# Revit family: LeL Tago 3.0
name_source: partatom
category: Lighting Fixtures
units: mm (PartAtom-declared; Revit-internal decimal feet)

## family parameters
Always vertical = No
Cut with Voids When Loaded = No
Light Source = No
OmniClass Number = 23.80.70.00
OmniClass Title = Lighting
Part Type = Normal
Room Calculation Point = No
Round Connector Dimension = Use Diameter
Shared = No
Work Plane-Based = Yes

## types (7) — shared parameters
Apparent Load = 14 VA
CCT = 3000 K
CRI = CRI80
Default Elevation = 1219 mm
Description = Outdoor/linear profiles
Finish = LeL Black
IK = IK09
IP = IP65 IP67 IP69
Lamp = LED
Manufacturer = L&L Luce&Light srl
Model = TG30
Rated Power supply = 230 V
URL = https://www.lucelight.it
Wattage = 14 W
Weight = 1.08 kg
zero-valued in all types: Clips offset

## per-type parameters (varying)
| type | Lumen Output | Optic |
| 3.0 A 14W | 664 lm | TAGO Light source : 3.0 A 14W |
| 3.0 G 14W | 682 lm | TAGO Light source : 3.0 G 14W |
| 3.0 K 69° 14W | 919 lm | TAGO Light source : 3.0 K 69° 14W |
| 3.0 L 29° 14W | 932 lm | TAGO Light source : 3.0 L 29° 14W |
| 3.0 M 17° 14W | 838 lm | TAGO Light source : 3.0 M 17° 14W |
| 3.0 S 11° 14W | 739 lm | TAGO Light source : 3.0 S 11° 14W |
| 3.0 W 20°x49° 14W | 851 lm | TAGO Light source : 3.0 W 20°x49° 14W |

## geometry (parser evidence)
native form markers: Sweep x4
no freeform markers — native parametric forms only
